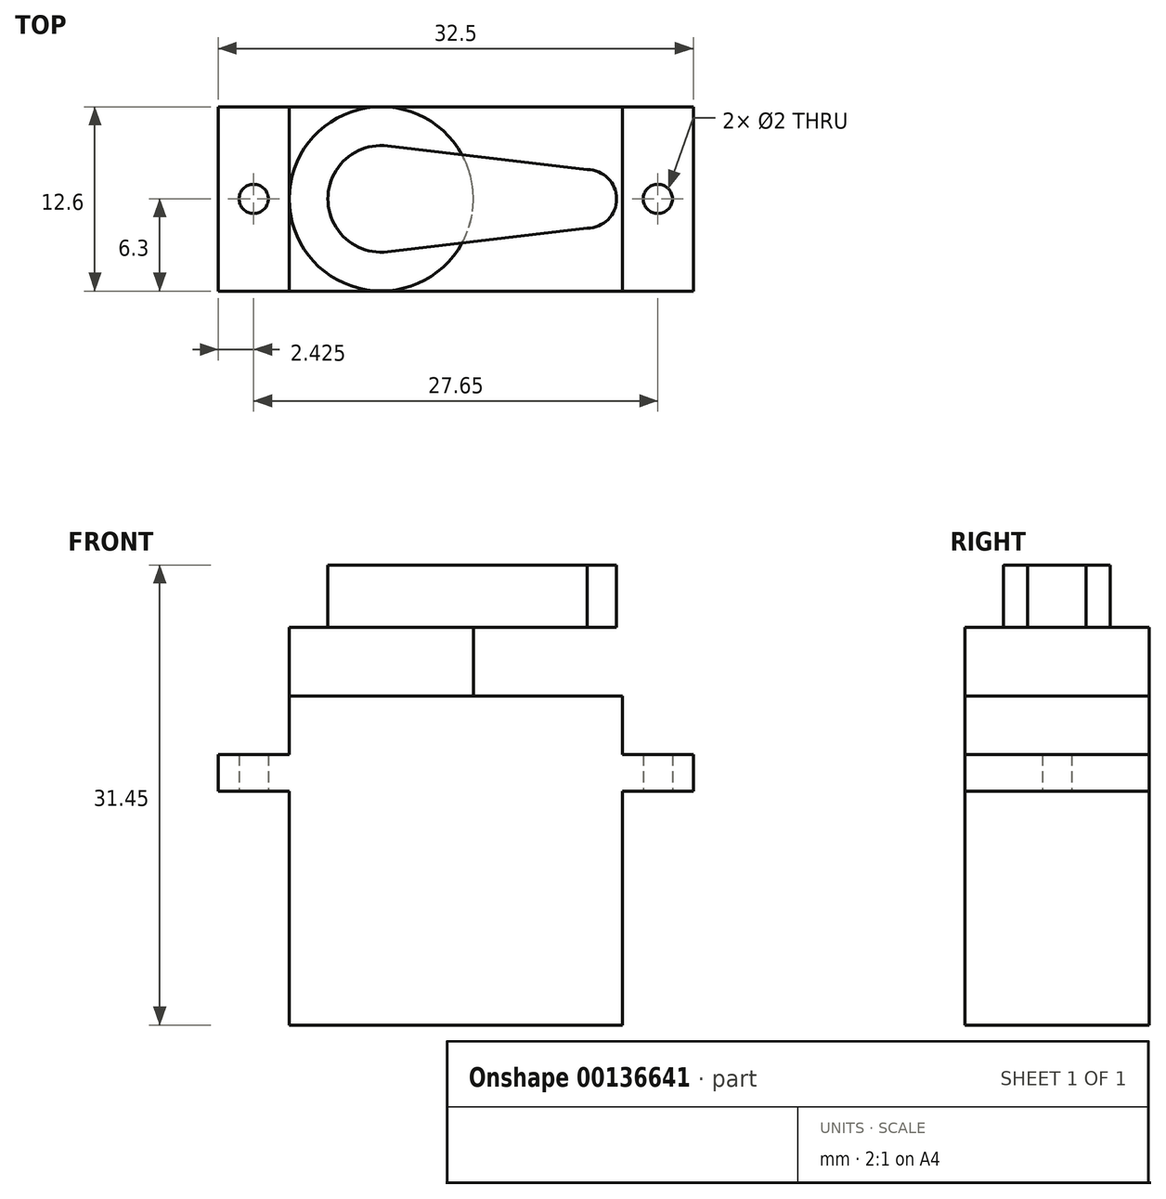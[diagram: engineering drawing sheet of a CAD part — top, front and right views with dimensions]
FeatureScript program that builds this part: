
annotation { "Feature Type Name" : "Feature", "Feature Type Description" : "" }
export const myFeature = defineFeature(function(context is Context, id is Id, definition is map)
    precondition{}
    {
        {
            assignVariable(context, id + "F0", {"name" : "servo_base_h", "anyValue" : 16});
        }
        {
            var Q0;
            Q0=qCreatedBy(makeId("Top.planeOp"),FACE);
            var sketch = newSketch(context, id + "F1", { "sketchPlane" : qUnion([Q0])});
            skLineSegment(sketch, "E0.bottom", {"start": v(11.4, 6.3) * mm, "end": v(-11.4, 6.3) * mm});
            skLineSegment(sketch, "E0.top", {"start": v(11.4, -6.3) * mm, "end": v(-11.4, -6.3) * mm});
            skLineSegment(sketch, "E0.left", {"start": v(11.4, 6.3) * mm, "end": v(11.4, -6.3) * mm});
            skLineSegment(sketch, "E0.right", {"start": v(-11.4, 6.3) * mm, "end": v(-11.4, -6.3) * mm});
            skPoint(sketch, "E0.middle", {"position": v(0, 0) * mm});
            skSolve(sketch);
        }
        {
            var Q0;
            Q0=makeQuery(id+"F1.imprint","IMPRINT",FACE,{"disambiguationData":[TD([[makeQuery(id+"F1.imprint","IMPRINT",EDGE,{"derivedFrom":sQuery(id+"F1.wireOp",EDGE,"E0.bottom")}),1.0]])]});
            var Q1;
            Q1 = qConstructionFilter(qBodyType(qCreatedBy(id + "F1" ,EDGE), BodyType.WIRE), ConstructionObject.NO);
            extrude(context, id + "F2", {"entities" : qUnion([Q0]), "surfaceEntities" : qUnion([Q1]), "depth" : (getVariable(context, 'servo_base_h')) * mm});
        }
        {
            assignVariable(context, id + "F3", {"name" : "servo_mount_h", "anyValue" : 2.5});
        }
        {
            var Q0;
            Q0=makeQuery(id+"F2.opExtrude","CAP_FACE",FACE,{"disambiguationData":[OSD([sQuery(id+"F1.wireOp",EDGE,"E0.bottom"),sQuery(id+"F1.wireOp",EDGE,"E0.top"),sQuery(id+"F1.wireOp",EDGE,"E0.left"),sQuery(id+"F1.wireOp",EDGE,"E0.right")])],"isStart":false});
            var sketch = newSketch(context, id + "F4", { "sketchPlane" : qUnion([Q0])});
            skLineSegment(sketch, "E1.bottom", {"start": v(16.25, 6.3) * mm, "end": v(-16.25, 6.3) * mm});
            skLineSegment(sketch, "E1.top", {"start": v(16.25, -6.3) * mm, "end": v(-16.25, -6.3) * mm});
            skLineSegment(sketch, "E1.left", {"start": v(16.25, 6.3) * mm, "end": v(16.25, -6.3) * mm});
            skLineSegment(sketch, "E1.right", {"start": v(-16.25, 6.3) * mm, "end": v(-16.25, -6.3) * mm});
            skPoint(sketch, "E1.middle", {"position": v(0, 0) * mm});
            skLineSegment(sketch, "E2", {"start": v(-16.25, 0) * mm, "end": v(-11.4, 0) * mm, "construction": true});
            skPoint(sketch, "E3", {"position": v(-13.83, 0) * mm});
            skLineSegment(sketch, "E4", {"start": v(16.25, 0) * mm, "end": v(11.4, 0) * mm, "construction": true});
            skPoint(sketch, "E5", {"position": v(13.82, 0) * mm});
            skCircle(sketch, "E6", {"center": v(-13.83, 0) * mm, "radius": 1 * mm});
            skCircle(sketch, "E7", {"center": v(13.82, 0) * mm, "radius": 1 * mm});
            skSolve(sketch);
        }
        {
            var Q0;
            Q0 = qSketchRegion(id + "F4", true);
            extrude(context, id + "F5", {"entities" : qUnion([Q0]), "operationType" : NewBodyOperationType.ADD, "depth" : (getVariable(context, 'servo_mount_h')) * mm});
        }
        {
            assignVariable(context, id + "F6", {"name" : "servo_top_h", "anyValue" : 4});
        }
        {
            var Q0;
            Q0=makeQuery(id+"F5.opExtrude","CAP_FACE",FACE,{"disambiguationData":[OSD([sQuery(id+"F4.wireOp",EDGE,"E1.bottom"),sQuery(id+"F4.wireOp",EDGE,"E1.top"),sQuery(id+"F4.wireOp",EDGE,"E1.left"),sQuery(id+"F4.wireOp",EDGE,"E1.right")])],"isStart":false});
            var sketch = newSketch(context, id + "F7", { "sketchPlane" : qUnion([Q0])});
            skLineSegment(sketch, "E8.0.0", {"start": v(11.4, -6.3) * mm, "end": v(11.4, 6.3) * mm});
            skLineSegment(sketch, "E8.0.1", {"start": v(11.4, 6.3) * mm, "end": v(-11.4, 6.3) * mm});
            skLineSegment(sketch, "E8.0.2", {"start": v(-11.4, 6.3) * mm, "end": v(-11.4, -6.3) * mm});
            skLineSegment(sketch, "E8.0.3", {"start": v(-11.4, -6.3) * mm, "end": v(11.4, -6.3) * mm});
            skSolve(sketch);
        }
        {
            var Q0;
            Q0 = qSketchRegion(id + "F7", true);
            extrude(context, id + "F8", {"entities" : qUnion([Q0]), "operationType" : NewBodyOperationType.ADD, "depth" : (getVariable(context, 'servo_top_h')) * mm});
        }
        {
            assignVariable(context, id + "F9", {"name" : "servo_top_gear_housing_h", "anyValue" : 4.7});
        }
        {
            var Q0;
            Q0=makeQuery(id+"F8.opExtrude","CAP_FACE",FACE,{"disambiguationData":[OSD([sQuery(id+"F7.wireOp",EDGE,"E8.0.0"),sQuery(id+"F7.wireOp",EDGE,"E8.0.1"),sQuery(id+"F7.wireOp",EDGE,"E8.0.2"),sQuery(id+"F7.wireOp",EDGE,"E8.0.3")])],"isStart":false});
            var sketch = newSketch(context, id + "F10", { "sketchPlane" : qUnion([Q0])});
            skCircle(sketch, "E9", {"center": v(-5.1, 0) * mm, "radius": 6.3 * mm});
            skSolve(sketch);
        }
        {
            var Q0;
            Q0 = qSketchRegion(id + "F10", true);
            extrude(context, id + "F11", {"entities" : qUnion([Q0]), "operationType" : NewBodyOperationType.ADD, "depth" : (getVariable(context, 'servo_top_gear_housing_h')) * mm});
        }
        {
            assignVariable(context, id + "F12", {"name" : "servo_arm_h", "anyValue" : 4.25});
        }
        {
            var Q0;
            Q0=makeQuery(id+"F11.opExtrude","CAP_FACE",FACE,{"disambiguationData":[OSD([sQuery(id+"F10.wireOp",EDGE,"E9")])],"isStart":false});
            var sketch = newSketch(context, id + "F13", { "sketchPlane" : qUnion([Q0])});
            skArc(sketch, "E10", {"start": v(-4.67, 3.62) * mm, "mid": v(-8.75, 0) * mm, "end": v(-4.67, -3.62) * mm});
            skLineSegment(sketch, "E11", {"start": v(-8.75, 0) * mm, "end": v(11, 0) * mm, "construction": true});
            skPoint(sketch, "E12", {"position": v(9, 0) * mm});
            skArc(sketch, "E13", {"start": v(9, -2) * mm, "mid": v(11, 0) * mm, "end": v(9, 2) * mm});
            skLineSegment(sketch, "E14", {"start": v(9, -2) * mm, "end": v(-4.67, -3.62) * mm});
            skLineSegment(sketch, "E15", {"start": v(9, 2) * mm, "end": v(-4.67, 3.62) * mm});
            skSolve(sketch);
        }
        {
            var Q0;
            Q0=makeQuery(id+"F13.imprint","IMPRINT",FACE,{"disambiguationData":[TD([[makeQuery(id+"F13.imprint","IMPRINT",EDGE,{"derivedFrom":sQuery(id+"F13.wireOp",EDGE,"E10")}),1.0]])]});
            var Q1;
            {var subQ0=sQuery(id+"F13.wireOp",EDGE,"E13");Q1=makeQuery(id+"F13.imprint","IMPRINT",FACE,{"disambiguationData":[TD([[makeQuery(id+"F13.imprint","IMPRINT",EDGE,{"derivedFrom":subQ0}),1.0]])]});}
            extrude(context, id + "F14", {"entities" : qUnion([Q0, Q1]), "depth" : (getVariable(context, 'servo_arm_h')) * mm});
        }
    });
